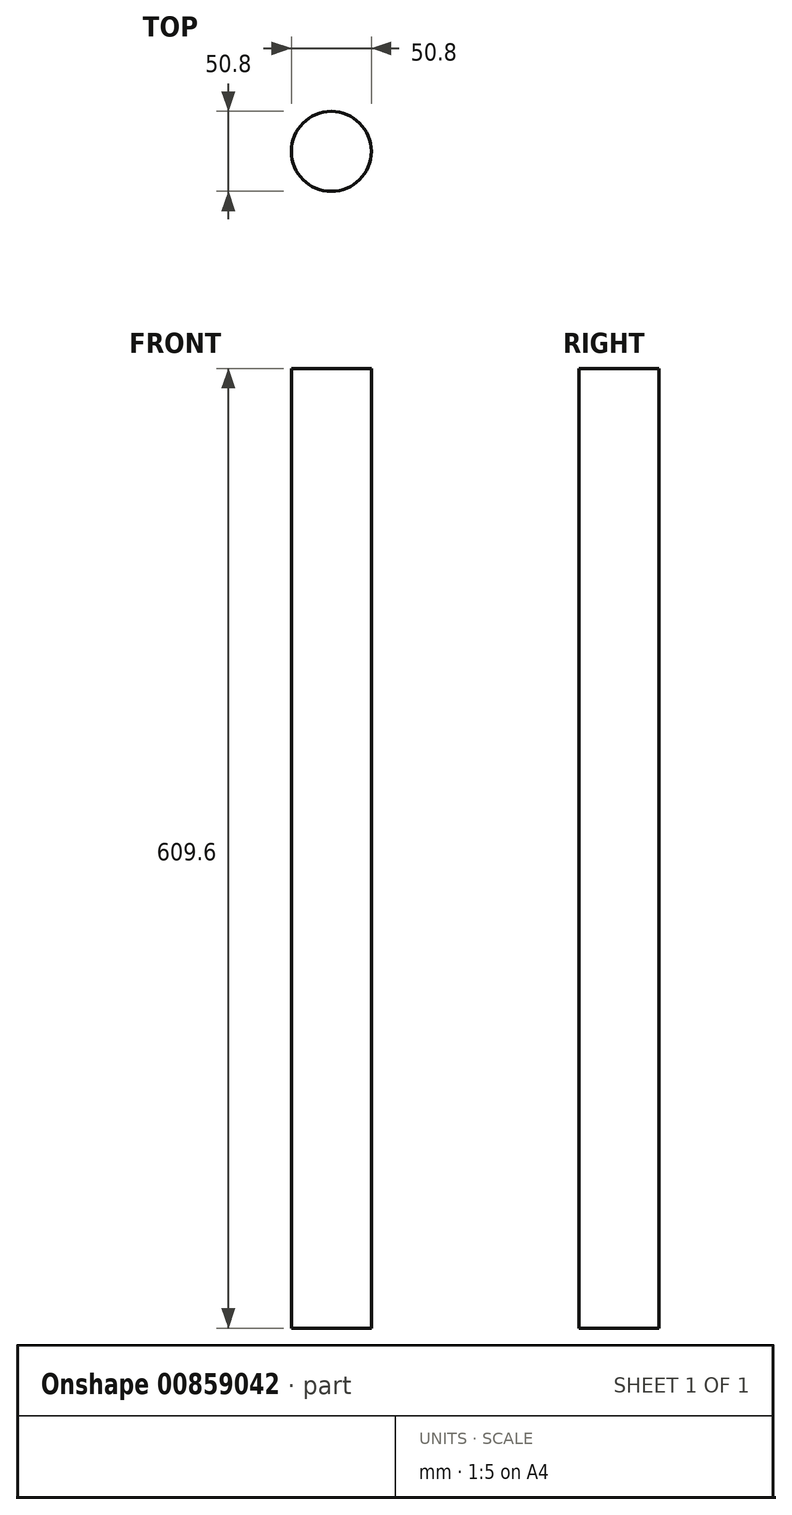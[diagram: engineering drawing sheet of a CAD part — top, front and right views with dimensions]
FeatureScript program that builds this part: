
annotation { "Feature Type Name" : "Feature", "Feature Type Description" : "" }
export const myFeature = defineFeature(function(context is Context, id is Id, definition is map)
    precondition{}
    {
        {
            var Q0;
            Q0=qCreatedBy(makeId("Top.planeOp"),FACE);
            var sketch = newSketch(context, id + "F0", { "sketchPlane" : qUnion([Q0])});
            skCircle(sketch, "E0", {"center": v(0, 0) * mm, "radius": 25.4 * mm});
            skSolve(sketch);
        }
        {
            var Q0;
            Q0 = qSketchRegion(id + "F0", true);
            extrude(context, id + "F1", {"entities" : qUnion([Q0]), "depth" : 609.6 * mm, "offsetDistance" : 25.4 * mm});
        }
    });
